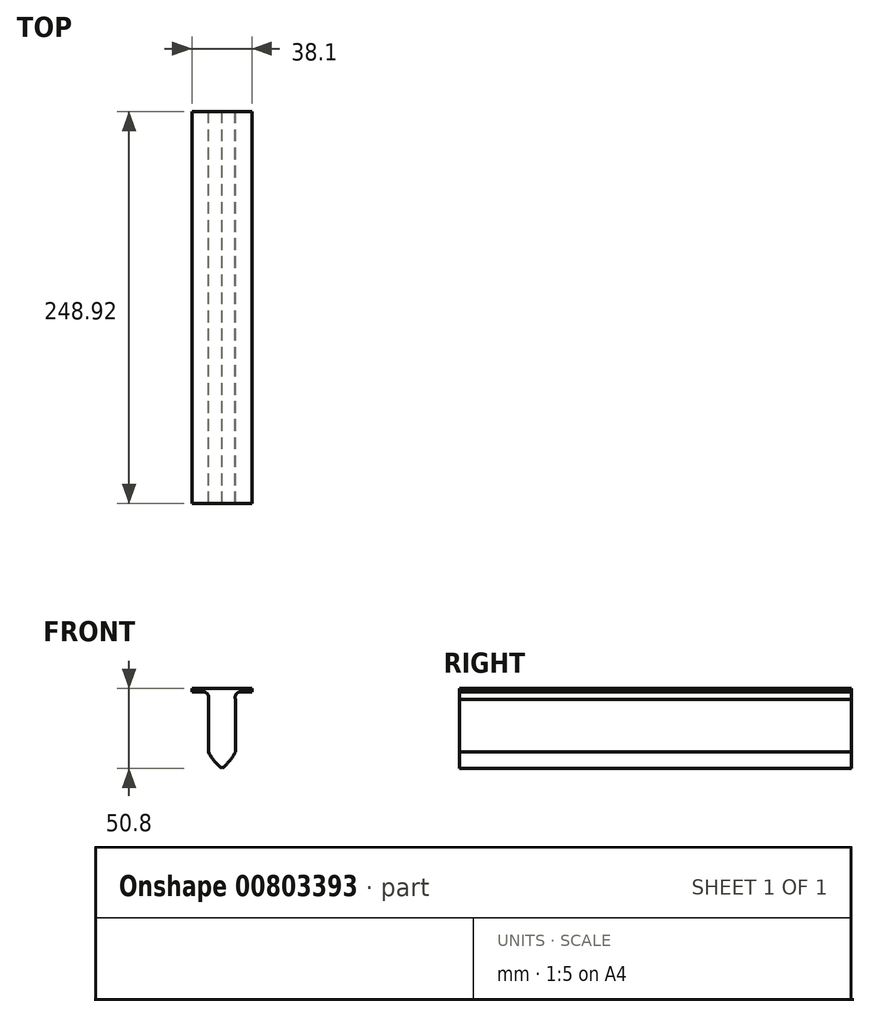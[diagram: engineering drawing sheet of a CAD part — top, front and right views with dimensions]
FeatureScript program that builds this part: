
annotation { "Feature Type Name" : "Feature", "Feature Type Description" : "" }
export const myFeature = defineFeature(function(context is Context, id is Id, definition is map)
    precondition{}
    {
        {
            var Q0;
            Q0=qCreatedBy(makeId("Front.planeOp"),FACE);
            var sketch = newSketch(context, id + "F0", { "sketchPlane" : qUnion([Q0])});
            skLineSegment(sketch, "E0.bottom", {"start": v(-19.05, 25.4) * mm, "end": v(19.05, 25.4) * mm});
            skLineSegment(sketch, "E0.top", {"start": v(-19.05, -25.4) * mm, "end": v(19.05, -25.4) * mm});
            skLineSegment(sketch, "E0.left", {"start": v(-19.05, 25.4) * mm, "end": v(-19.05, -25.4) * mm});
            skLineSegment(sketch, "E0.right", {"start": v(19.05, 25.4) * mm, "end": v(19.05, -25.4) * mm});
            skLineSegment(sketch, "E1", {"start": v(-19.05, 23.3) * mm, "end": v(-12.06, 23.3) * mm});
            skArc(sketch, "E2", {"start": v(-8.57, 18.47) * mm, "mid": v(-9.08, 21.78) * mm, "end": v(-12.06, 23.3) * mm});
            skLineSegment(sketch, "E3", {"start": v(-8.57, 18.47) * mm, "end": v(-8.57, -15.06) * mm});
            skLineSegment(sketch, "E4", {"start": v(0, 0) * mm, "end": v(0, 10.15) * mm});
            skLineSegment(sketch, "E5.MirrorCS", {"start": v(19.05, 23.3) * mm, "end": v(12.06, 23.3) * mm});
            skArc(sketch, "E6.MirrorCS", {"start": v(8.57, 18.47) * mm, "mid": v(9.08, 21.78) * mm, "end": v(12.06, 23.3) * mm});
            skLineSegment(sketch, "E7.MirrorCS", {"start": v(8.57, 18.47) * mm, "end": v(8.57, -15.06) * mm});
            skArc(sketch, "E8", {"start": v(-8.57, -15.06) * mm, "mid": v(-4.84, -20.7) * mm, "end": v(0, -25.4) * mm});
            skArc(sketch, "E9.MirrorCS", {"start": v(8.57, -15.06) * mm, "mid": v(4.84, -20.7) * mm, "end": v(0, -25.4) * mm});
            skSolve(sketch);
        }
        {
            var Q0;
            {var subQ1=sQuery(id+"F0.wireOp",EDGE,"E0.bottom");Q0=makeQuery(id+"F0.imprint","IMPRINT",FACE,{"disambiguationData":[TD([[makeQuery(id+"F0.imprint","IMPRINT",EDGE,{"derivedFrom":subQ1}),-1.0]])]});}
            extrude(context, id + "F1", {"entities" : qUnion([Q0]), "depth" : 248.92 * mm, "offsetDistance" : 25.4 * mm});
        }
    });
